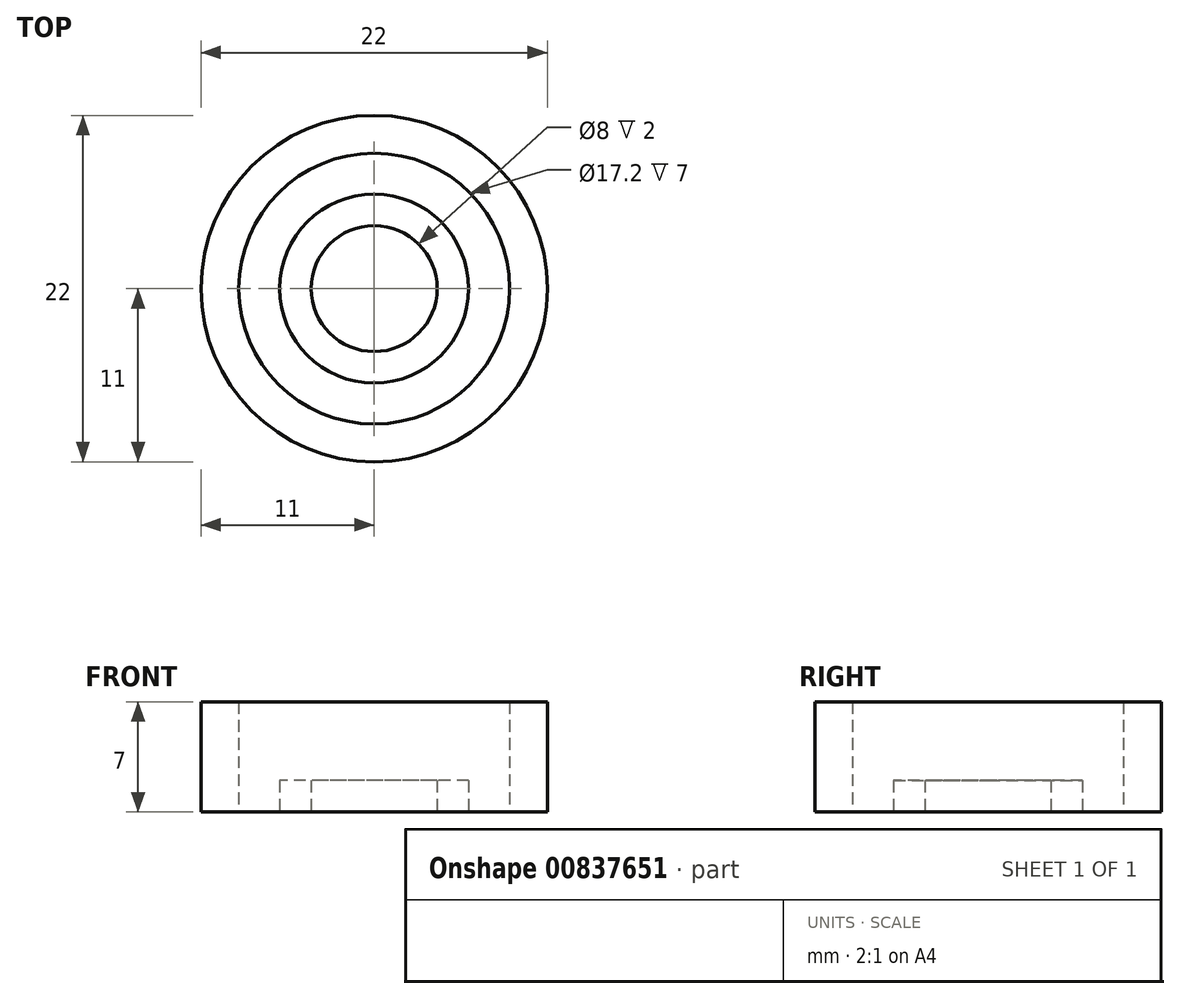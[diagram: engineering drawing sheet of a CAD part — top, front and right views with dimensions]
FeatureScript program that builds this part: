
annotation { "Feature Type Name" : "Feature", "Feature Type Description" : "" }
export const myFeature = defineFeature(function(context is Context, id is Id, definition is map)
    precondition{}
    {
        {
            var Q0;
            Q0=qCreatedBy(makeId("Top.planeOp"),FACE);
            var sketch = newSketch(context, id + "F0", { "sketchPlane" : qUnion([Q0])});
            skCircle(sketch, "E0", {"center": v(0, 0) * mm, "radius": 11 * mm});
            skSolve(sketch);
        }
        {
            var Q0;
            Q0=makeQuery(id+"F0.imprint","IMPRINT",FACE,{"disambiguationData":[TD([[makeQuery(id+"F0.imprint","IMPRINT",EDGE,{"derivedFrom":sQuery(id+"F0.wireOp",EDGE,"E0")}),1.0]])]});
            extrude(context, id + "F1", {"entities" : qUnion([Q0]), "depth" : 7 * mm, "offsetDistance" : 25 * mm});
        }
        {
            var Q0;
            Q0=qCreatedBy(makeId("Top.planeOp"),FACE);
            var sketch = newSketch(context, id + "F2", { "sketchPlane" : qUnion([Q0])});
            skCircle(sketch, "E1", {"center": v(0, 0) * mm, "radius": 8.6 * mm});
            skSolve(sketch);
        }
        {
            var Q0;
            Q0 = qSketchRegion(id + "F2", true);
            extrude(context, id + "F3", {"entities" : qUnion([Q0]), "operationType" : NewBodyOperationType.REMOVE, "depth" : 18.2 * mm, "offsetDistance" : 25 * mm});
        }
        {
            var Q0;
            Q0=qCreatedBy(makeId("Top.planeOp"),FACE);
            var sketch = newSketch(context, id + "F4", { "sketchPlane" : qUnion([Q0])});
            skCircle(sketch, "E2", {"center": v(0, 0) * mm, "radius": 4 * mm});
            skCircle(sketch, "E3", {"center": v(0, 0) * mm, "radius": 6 * mm});
            skSolve(sketch);
        }
        {
            var Q0;
            Q0=makeQuery(id+"F4.imprint","IMPRINT",FACE,{"disambiguationData":[TD([[makeQuery(id+"F4.imprint","IMPRINT",EDGE,{"derivedFrom":sQuery(id+"F4.wireOp",EDGE,"E2")}),-1.0]])]});
            extrude(context, id + "F5", {"entities" : qUnion([Q0]), "depth" : 2 * mm, "offsetDistance" : 25 * mm});
        }
    });
